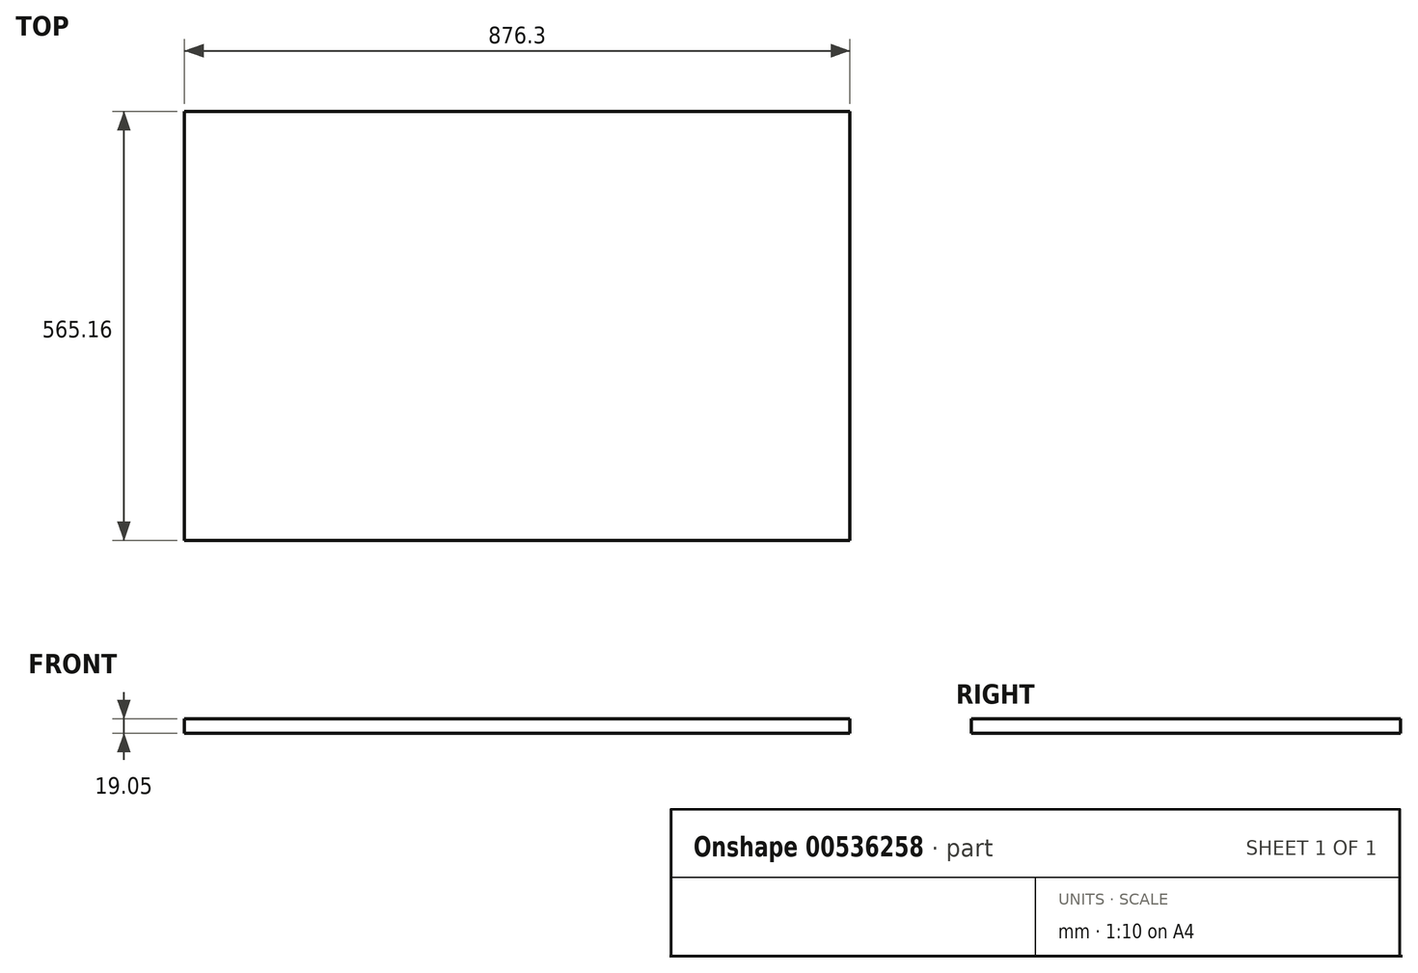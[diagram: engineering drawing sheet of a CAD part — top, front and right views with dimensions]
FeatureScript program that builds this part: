
annotation { "Feature Type Name" : "Feature", "Feature Type Description" : "" }
export const myFeature = defineFeature(function(context is Context, id is Id, definition is map)
    precondition{}
    {
        {
            var Q0;
            Q0=qCreatedBy(makeId("Top.planeOp"),FACE);
            var sketch = newSketch(context, id + "F0", { "sketchPlane" : qUnion([Q0])});
            skLineSegment(sketch, "E0.bottom", {"start": v(428.62, 282.58) * mm, "end": v(-428.63, 282.57) * mm});
            skLineSegment(sketch, "E0.top", {"start": v(428.63, -282.57) * mm, "end": v(-428.62, -282.58) * mm});
            skLineSegment(sketch, "E0.left", {"start": v(428.62, 282.58) * mm, "end": v(428.63, -282.57) * mm});
            skLineSegment(sketch, "E0.right", {"start": v(-428.63, 282.57) * mm, "end": v(-428.62, -282.58) * mm});
            skPoint(sketch, "E0.middle", {"position": v(0, 0) * mm});
            skSolve(sketch);
        }
        {
            var Q0;
            Q0=makeQuery(id+"F0.imprint","IMPRINT",FACE,{"disambiguationData":[TD([[makeQuery(id+"F0.imprint","IMPRINT",EDGE,{"derivedFrom":sQuery(id+"F0.wireOp",EDGE,"E0.bottom")}),1.0]])]});
            extrude(context, id + "F1", {"entities" : qUnion([Q0]), "depth" : 19.05 * mm, "offsetDistance" : 25.4 * mm});
        }
        {
            var Q0;
            Q0=makeQuery(id+"F1.opExtrude","SWEPT_FACE",FACE,{"disambiguationData":[OSD([sQuery(id+"F0.wireOp",EDGE,"E0.left")])]});
            extrude(context, id + "F2", {"entities" : qUnion([Q0]), "operationType" : NewBodyOperationType.ADD, "depth" : 19.05 * mm, "offsetDistance" : 25.4 * mm});
        }
    });
